# Revit family: CENTUM Doppel-Rollenlager, axial, 114-273 mm
name_source: partatom
category: Allgemeines Modell
revit_build: Autodesk Revit 2018 (Build: 20190510_1515(x64)
units: mm (PartAtom-declared; Revit-internal decimal feet)

## family parameters
Arbeitsebenenbasiert = Ja
Beim Laden mit Abzugskörper schneiden = Nein
Bemaßung runder Anschluss = Durchmesser verwenden
Gemeinsam genutzt = Ja
Immer vertikal = Nein
Kann Basisbauteil für Bewehrung sein = Nein
Raumberechnungspunkt = Nein
Teiletyp = Normal

## types (3) — shared parameters
Breite mit Laschen = 100 mm
Fabrikat = MEFA
Höhe = 76 mm
Kurztext1 = Rollenlager doppel axial
Lasttyp = DR 003
Lochabstand längs = 80 mm  [stored 0.262467 ft]
Lochabstand quer = 80 mm  [stored 0.262467 ft]
Länge = 170 mm  [stored 0.557743 ft]
Material = Stahl
Mengeneinheit = St
Sicherheitsfaktor = 1.54
Stärke Material = 3 mm  [stored 0.00984252 ft]
Vorgabe-Ansicht = 1219 mm
max. Auflagenbreite = 273 mm
max. zul. Last = 3.00 kN
min. Auflagenbreite = 114 mm
vpe = 1

## per-type parameters (varying)
| type | Artikelnummer | EAN | Gewicht | Gewicht pro Bauteil | Kurztext2 |
| Rollenlager doppel Axial, 114-273 mm roh | 150dr030273 | 4250928435217 | 1.89 kg | 1.89 kg | 114 - 273 mm 3 kN roh |
| Rollenlager doppel Axial, 114-273 mm gvz | 150dg030273 | 4250928435088 | 1.89 kg | 1.89 kg | 114 - 273 mm 3 kN gvz |
| Rollenlager doppel Axial, 114-273 mm fsv | 150df030273 | 4250928434951 | 1.98 kg | 1.98 kg | 114 - 273 mm 3 kN fsv |

note: [stored X ft] marks values corroborated as IEEE doubles in the binary element streams (Revit-internal decimal feet)
